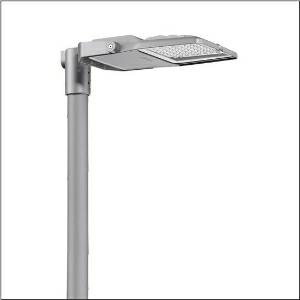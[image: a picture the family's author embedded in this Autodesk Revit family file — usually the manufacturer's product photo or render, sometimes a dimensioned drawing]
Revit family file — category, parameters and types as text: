
# Revit family: floodlight_fl_21_mini___pl61_5xa7775b2c3a_8a89
name_source: partatom
category: Lighting Fixtures
units: mm (PartAtom-declared; Revit-internal decimal feet)

## family parameters
Cut with Voids When Loaded = No
Host = Face
Light Source = No
Part Type = Normal
Room Calculation Point = No
Round Connector Dimension = Use Diameter
Shared = No

## types (1)
- --- (1 x LED, 6110 lm, 45.7 W, 3000K)
    Apparent Load = 46 VA
    CIE Flux Codes = 33 65 98 100 100
    Color Rendering = 70
    Color Temperature = 3000K
    Default Elevation = 1800 mm
    Description = Floodlight FL 21 mini, floodlight, primary light control with lens, of PMMA, primary optical cover: protective disc, of toughened safety glass, transparent, light distribution: PL61, light emission: direct distribution, installation type: surface-mounted, LED, High Power LED, rated luminous flux: 6.110lm, luminous efficacy: 134lm/W, light colour: 730, colour temperature: 3000K, control gear: Smart Interface (Zhaga), control: flexible luminous flux parameterisation, time-dependent luminous flux control, constant luminous flux control, overheat protection, pre-setting: logarithmic dimming characteristic, with terminal, 6-pole, mains connection: 220..240V, AC, 50/60Hz, start of lifetime: 46W, end of service life: 48W, reduction: 22W, luminaire housing, of diecast aluminium, powder-coated, SITECO metallic grey (DB 702S), corrosivity category C5 mid according to DIN EN ISO 12944, suitable for swimming pools, chlorine-resistant, sealing non-destructively replaceable, please order mast flange separately, mast bracket, of steel, galvanised, powder-coated, SITECO metallic grey (DB 702S), Smart Interface above, protection rating (complete): IP66, insulation class (complete): insulation class II (safety insulation), certification: CE, ENEC, VDE, protection symbol: D, impact resistance: IK08, permissible operating ambient temperature: -40..+40°C, permissible operating ambient temperature for outdoor applications: -40..+50°C, standard: DIN EN 12944, LABS conformity tested according to VDMA 24364:2018-05, packaging unit: 1 piece

Light Distribution: PL61
    Height = 70 mm
    Lamp = 1 x LED
    Lamp Light Flux = 6110 lm
    Lamp Power = 45.7 W
    Lamp count = 1
    Length = 485 mm
    Luminous efficacy = 134 lm/W
    Manufacturer = Siteco
    ModVariant = No
    Model = 5XA7775B2C3A
    Number of Poles = 1
    OnlyDefault = Yes
    Power Factor = 1
    Product Name = Floodlight FL 21 mini | PL61
    Product group = floodlight | pylon annexe
    ProductGroupID = 6201
    Protection Class = Protection class II
    Protection Degree = IP 66
    RLX_Detail_Level = 1
    RLX_Emergency_Light_Flux = 0 lm
    RLX_Emergency_Type = 0
    RLX_Emergency_Type_DB = No
    RlxData = <blob elided: 101037 chars, md5=d2c83077>
    Socket = socket
    Standby Power = 0 W
    System Light Flux = 6110 lm
    System Power = 46 W
    Type Comments = factory setting: luminous flux: 100 % | dim-lin: 254 | 463 mA
    Type Image = l_1007125.jpg
    URL = http://relux.com
    VarID = @adj_171679
    Voltage = 0 V
    Weight = 0.00 kg
    Width = 337 mm

## geometry (parser evidence)
native form markers: Blend x4, Sweep x14
no freeform markers — native parametric forms only
